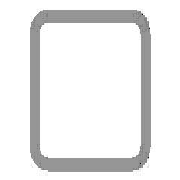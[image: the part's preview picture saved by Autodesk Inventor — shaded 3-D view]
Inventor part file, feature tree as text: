
AUTODESK INVENTOR PART (.ipt)
format: ipt  version: 2024 (Build 280153000, 153)  size: 143,872 bytes
history: native  units: mm (DEFAULTED — no unit token found)
features: other x4, plane x2, extrude x1, split x1, sketch x1
ambient origin geometry x8: Origin, YZ Plane, XZ Plane, XY Plane, X Axis, Y Axis, Z Axis, Center Point
bodies: Solid1 (feature_tree)
feature tree (9):
  parser-record x1  (decoder bookkeeping rows leaked as tree rows — omitted from the tree; the rows remain in map.json)
  other  "Driven Length"
  other  "Plano inicial"
  other  "Plano final"
  extrude  "Cuerpo"  TaperAngle=0.0deg  [1 undecoded]
  plane  "Plano de trabajo4"
  split  "Dividir1"
  sketch  "Sketch3"  dims[d3=255.4mm d4=0.0mm d10=50.8mm d11=50.8mm d12=3.175mm d13=-25.4mm d14=230.0mm d15=25.4mm d16=25.4mm d17=6.35mm d18=90.0deg d19=255.4mm]
  plane  "Work Plane3"
note: 1 required parameter value undecoded (feature->parameter linkage not recoverable at this tier; creation-order binding heuristic only, values carry confidence <= 0.55)
